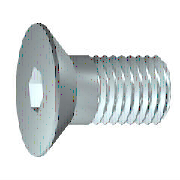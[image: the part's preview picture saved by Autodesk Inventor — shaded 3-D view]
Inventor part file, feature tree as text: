
AUTODESK INVENTOR PART (.ipt)
format: ipt  version: 2019 (Build 230136000, 136)  size: 180,736 bytes
history: native  units: mm (DEFAULTED — no unit token found)
features: sketch x2, extrude x1, plane x1
ambient origin geometry x7: Origin, YZ Plane, XY Plane, X Axis, Y Axis, Z Axis, Center Point
bodies: Solid1 (feature_tree), Body (feature_tree)
feature tree (4):
  sketch  "Sketch2"  dims[d2=1.78mm d3=4.0mm d6=2.48mm d7=45.0deg d8=2.886751mm d9=60.0deg d10=7.53mm d11=4.0mm d12=0.429415mm d13=90.0deg d30=10.0mm d14=0.0mm d15=11.0mm d16=0.0mm d17=0.429415mm d18=0.429415mm d20=0.0mm d39=45.0deg d43=0.0mm d44=0.0mm]
  extrude  "Slot"  Depth=11.0mm
  plane  "Work Plane1"
  sketch  "Sketch1"  dims[d0=16.0mm d1=11.0mm]
